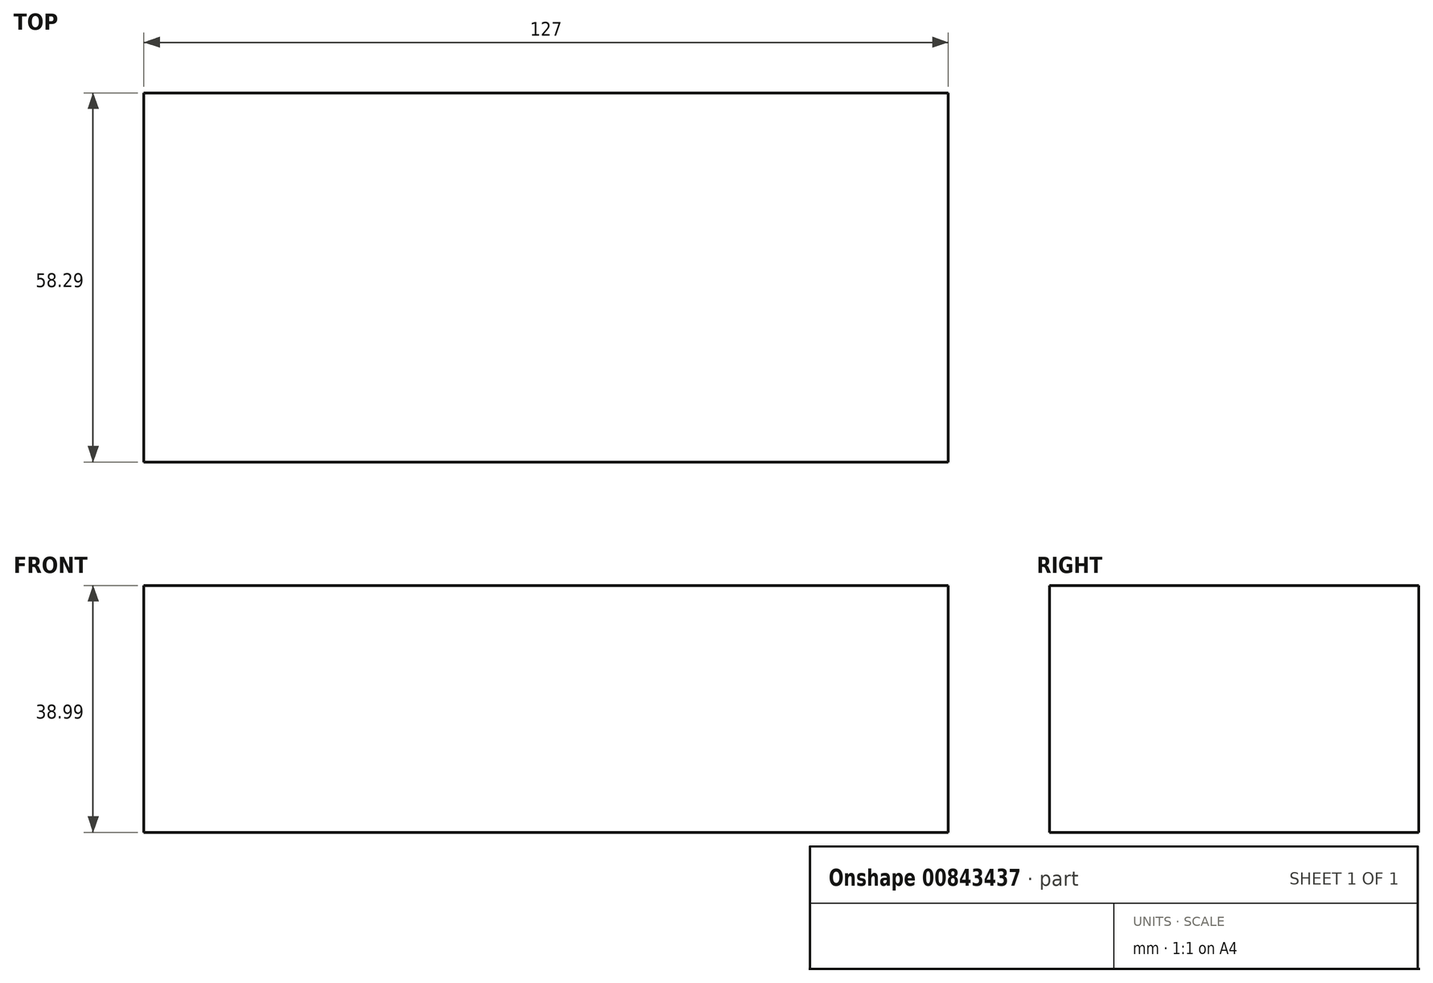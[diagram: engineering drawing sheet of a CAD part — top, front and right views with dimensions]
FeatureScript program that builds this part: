
annotation { "Feature Type Name" : "Feature", "Feature Type Description" : "" }
export const myFeature = defineFeature(function(context is Context, id is Id, definition is map)
    precondition{}
    {
        {
            var Q0;
            Q0=qCreatedBy(makeId("Right.planeOp"),FACE);
            var sketch = newSketch(context, id + "F0", { "sketchPlane" : qUnion([Q0])});
            skLineSegment(sketch, "E0", {"start": v(0, 0) * mm, "end": v(58.3, 0) * mm});
            skLineSegment(sketch, "E1", {"start": v(58.3, 0) * mm, "end": v(58.3, 38.99) * mm});
            skLineSegment(sketch, "E2", {"start": v(58.3, 38.99) * mm, "end": v(0, 38.99) * mm});
            skLineSegment(sketch, "E3", {"start": v(0, 38.99) * mm, "end": v(0, 0) * mm});
            skSolve(sketch);
        }
        {
            var Q0;
            Q0 = qSketchRegion(id + "F0", true);
            extrude(context, id + "F1", {"entities" : qUnion([Q0]), "endBound" : BoundingType.SYMMETRIC, "depth" : 127 * mm, "offsetDistance" : 25.4 * mm});
        }
    });
